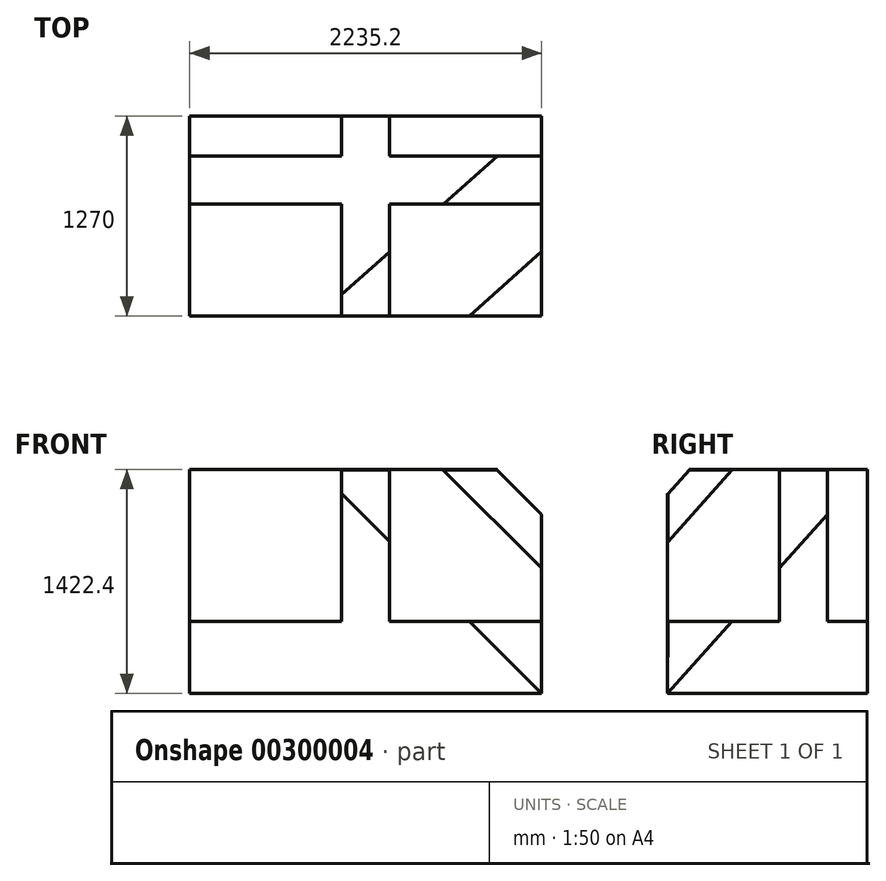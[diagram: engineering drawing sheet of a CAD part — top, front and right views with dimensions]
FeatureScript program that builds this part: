
annotation { "Feature Type Name" : "Feature", "Feature Type Description" : "" }
export const myFeature = defineFeature(function(context is Context, id is Id, definition is map)
    precondition{}
    {
        {
            var Q0;
            Q0=qCreatedBy(makeId("Top.planeOp"),FACE);
            var sketch = newSketch(context, id + "F0", { "sketchPlane" : qUnion([Q0])});
            skLineSegment(sketch, "E0.bottom", {"start": v(0, 0) * mm, "end": v(-2235.2, 0) * mm});
            skLineSegment(sketch, "E0.top", {"start": v(0, 1270) * mm, "end": v(-2235.2, 1270) * mm});
            skLineSegment(sketch, "E0.left", {"start": v(0, 0) * mm, "end": v(0, 1270) * mm});
            skLineSegment(sketch, "E0.right", {"start": v(-2235.2, 0) * mm, "end": v(-2235.2, 1270) * mm});
            skLineSegment(sketch, "E1", {"start": v(-1270, 1270) * mm, "end": v(-1270, 1016) * mm});
            skLineSegment(sketch, "E2", {"start": v(-1270, 1016) * mm, "end": v(-2235.2, 1016) * mm});
            skLineSegment(sketch, "E3", {"start": v(-2235.2, 1016) * mm, "end": v(-2235.2, 711.2) * mm});
            skLineSegment(sketch, "E4", {"start": v(-2235.2, 711.2) * mm, "end": v(-1270, 711.2) * mm});
            skLineSegment(sketch, "E5", {"start": v(-1270, 711.2) * mm, "end": v(-1270, 0) * mm});
            skLineSegment(sketch, "E6", {"start": v(-1270, 0) * mm, "end": v(-965.2, 0) * mm});
            skLineSegment(sketch, "E7", {"start": v(-965.2, 0) * mm, "end": v(-965.2, 711.2) * mm});
            skLineSegment(sketch, "E8", {"start": v(-965.2, 711.2) * mm, "end": v(0, 711.2) * mm});
            skLineSegment(sketch, "E9", {"start": v(0, 711.2) * mm, "end": v(0, 1016) * mm});
            skLineSegment(sketch, "E10", {"start": v(0, 1016) * mm, "end": v(-965.2, 1016) * mm});
            skLineSegment(sketch, "E11", {"start": v(-965.2, 1016) * mm, "end": v(-965.2, 1270) * mm});
            skLineSegment(sketch, "E12", {"start": v(-965.2, 1270) * mm, "end": v(-1270, 1270) * mm});
            skSolve(sketch);
        }
        {
            var Q0;
            Q0=makeQuery(id+"F0.imprint","IMPRINT",FACE,{"disambiguationData":[TD([[makeQuery(id+"F0.imprint","IMPRINT",EDGE,{"derivedFrom":sQuery(id+"F0.wireOp",EDGE,"E1")}),1.0]])]});
            extrude(context, id + "F1", {"entities" : qUnion([Q0]), "depth" : 1422.4 * mm});
        }
        {
            var Q0;
            {var subQ3=sQuery(id+"F0.wireOp",EDGE,"E1");Q0=makeQuery(id+"F0.imprint","IMPRINT",FACE,{"disambiguationData":[TD([[makeQuery(id+"F0.imprint","IMPRINT",EDGE,{"derivedFrom":subQ3}),-1.0]])]});}
            var Q1;
            {var subQ4=sQuery(id+"F0.wireOp",EDGE,"E10");Q1=makeQuery(id+"F0.imprint","IMPRINT",FACE,{"disambiguationData":[TD([[makeQuery(id+"F0.imprint","IMPRINT",EDGE,{"derivedFrom":subQ4}),-1.0]])]});}
            var Q2;
            {var subQ4=sQuery(id+"F0.wireOp",EDGE,"E4");Q2=makeQuery(id+"F0.imprint","IMPRINT",FACE,{"disambiguationData":[TD([[makeQuery(id+"F0.imprint","IMPRINT",EDGE,{"derivedFrom":subQ4}),-1.0]])]});}
            var Q3;
            {var subQ3=sQuery(id+"F0.wireOp",EDGE,"E7");Q3=makeQuery(id+"F0.imprint","IMPRINT",FACE,{"disambiguationData":[TD([[makeQuery(id+"F0.imprint","IMPRINT",EDGE,{"derivedFrom":subQ3}),-1.0]])]});}
            extrude(context, id + "F2", {"entities" : qUnion([Q0, Q1, Q2, Q3]), "operationType" : NewBodyOperationType.ADD, "depth" : 457.2 * mm});
        }
        {
            var Q0;
            {var subQ0=sQuery(id+"F0.wireOp",EDGE,"E0.left");var subQ1=sQuery(id+"F0.wireOp",EDGE,"E9");Q0=makeQuery(id+"F2.boolean.opBoolean","MERGE",FACE,{"derivedFrom":[makeQuery(id+"F1.opExtrude","SWEPT_FACE",FACE,{"disambiguationData":[OSD([subQ1])]}),makeQuery(id+"F2.opExtrude","SWEPT_FACE",FACE,{"disambiguationData":[OSD([subQ0]),TDD([makeQuery(id+"F0.imprint","IMPRINT",EDGE,{"disambiguationData":[TD([[makeQuery(id+"F0.imprint","INTERSECT",VERTEX,{"derivedFrom":[sQuery(id+"F0.wireOp",EDGE,"E0.bottom"),subQ0]}),-1.0]])],"derivedFrom":subQ0})])]}),makeQuery(id+"F2.opExtrude","SWEPT_FACE",FACE,{"disambiguationData":[OSD([subQ0]),TDD([makeQuery(id+"F0.imprint","IMPRINT",EDGE,{"disambiguationData":[TD([[makeQuery(id+"F0.imprint","INTERSECT",VERTEX,{"derivedFrom":[sQuery(id+"F0.wireOp",EDGE,"E0.top"),subQ0]}),1.0]])],"derivedFrom":subQ0})])]})]});}
            var sketch = newSketch(context, id + "F3", { "sketchPlane" : qUnion([Q0])});
            skPoint(sketch, "E13", {"position": v(1270, 1422.4) * mm});
            skLineSegment(sketch, "E14", {"start": v(0, 0) * mm, "end": v(1270, 1422.4) * mm});
            skSolve(sketch);
        }
        {
            var Q0;
            {var subQ0=sQuery(id+"F0.wireOp",EDGE,"E0.bottom");var subQ1=sQuery(id+"F0.wireOp",EDGE,"E6");Q0=makeQuery(id+"F2.boolean.opBoolean","MERGE",FACE,{"derivedFrom":[makeQuery(id+"F1.opExtrude","SWEPT_FACE",FACE,{"disambiguationData":[OSD([subQ1])]}),makeQuery(id+"F2.opExtrude","SWEPT_FACE",FACE,{"disambiguationData":[OSD([subQ0]),TDD([makeQuery(id+"F0.imprint","IMPRINT",EDGE,{"disambiguationData":[TD([[makeQuery(id+"F0.imprint","INTERSECT",VERTEX,{"derivedFrom":[subQ0,sQuery(id+"F0.wireOp",EDGE,"E0.left")]}),-1.0]])],"derivedFrom":subQ0})])]}),makeQuery(id+"F2.opExtrude","SWEPT_FACE",FACE,{"disambiguationData":[OSD([subQ0]),TDD([makeQuery(id+"F0.imprint","IMPRINT",EDGE,{"disambiguationData":[TD([[makeQuery(id+"F0.imprint","INTERSECT",VERTEX,{"derivedFrom":[subQ0,sQuery(id+"F0.wireOp",EDGE,"E0.right")]}),1.0]])],"derivedFrom":subQ0})])]})]});}
            var sketch = newSketch(context, id + "F4", { "sketchPlane" : qUnion([Q0])});
            skLineSegment(sketch, "E15", {"start": v(0, 0) * mm, "end": v(-1422.4, 1422.4) * mm});
            skSolve(sketch);
        }
        {
            var Q0;
            Q0=makeQuery(id+"F1.opExtrude","CAP_FACE",FACE,{"disambiguationData":[OSD([sQuery(id+"F0.wireOp",EDGE,"E1"),sQuery(id+"F0.wireOp",EDGE,"E2"),sQuery(id+"F0.wireOp",EDGE,"E3"),sQuery(id+"F0.wireOp",EDGE,"E4"),sQuery(id+"F0.wireOp",EDGE,"E5"),sQuery(id+"F0.wireOp",EDGE,"E6"),sQuery(id+"F0.wireOp",EDGE,"E7"),sQuery(id+"F0.wireOp",EDGE,"E8"),sQuery(id+"F0.wireOp",EDGE,"E9"),sQuery(id+"F0.wireOp",EDGE,"E10"),sQuery(id+"F0.wireOp",EDGE,"E11"),sQuery(id+"F0.wireOp",EDGE,"E12")])],"isStart":false});
            var sketch = newSketch(context, id + "F5", { "sketchPlane" : qUnion([Q0])});
            skLineSegment(sketch, "E16", {"start": v(-1426.98, 0) * mm, "end": v(0, 1270.66) * mm});
            skSolve(sketch);
        }
        {
            var Q0;
            Q0=sQuery(id+"F5.wireOp",VERTEX,"E16.start");
            var Q1;
            Q1=sQuery(id+"F3.wireOp",VERTEX,"E13");
            var Q2;
            Q2=sQuery(id+"F4.wireOp",VERTEX,"E15.start");
            cPlane(context, id + "F6", {"entities" : qUnion([Q0, Q1, Q2]), "cplaneType" : CPlaneType.THREE_POINT, "offset" : 0 * mm, "width" : 152.4 * mm, "height" : 152.4 * mm});
        }
        {
            var Q0;
            Q0=qCreatedBy(id+"F6.planeOp",FACE);
            var sketch = newSketch(context, id + "F7", { "sketchPlane" : qUnion([Q0])});
            skLineSegment(sketch, "E17", {"start": v(0, 1904.37) * mm, "end": v(0, 0) * mm});
            skLineSegment(sketch, "E18", {"start": v(0, 0) * mm, "end": v(-1709, 1061.02) * mm});
            skLineSegment(sketch, "E19", {"start": v(-1709, 1061.02) * mm, "end": v(0, 1904.37) * mm});
            skSolve(sketch);
        }
        {
            var Q0;
            Q0 = qSketchRegion(id + "F7", true);
            extrude(context, id + "F8", {"entities" : qUnion([Q0]), "operationType" : NewBodyOperationType.REMOVE, "depth" : 508 * mm});
        }
    });
